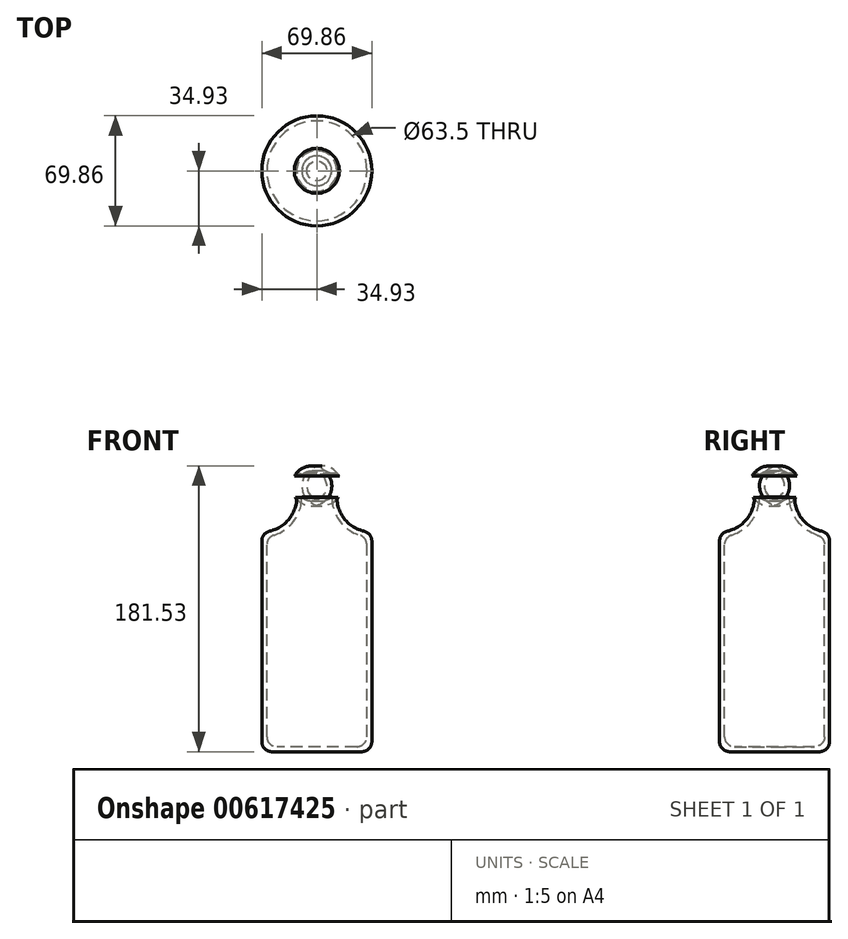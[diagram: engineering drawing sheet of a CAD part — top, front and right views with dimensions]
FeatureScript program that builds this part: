
annotation { "Feature Type Name" : "Feature", "Feature Type Description" : "" }
export const myFeature = defineFeature(function(context is Context, id is Id, definition is map)
    precondition{}
    {
        {
            var Q0;
            Q0=qCreatedBy(makeId("Front.planeOp"),FACE);
            var sketch = newSketch(context, id + "F0", { "sketchPlane" : qUnion([Q0])});
            skLineSegment(sketch, "E0", {"start": v(0, 0) * mm, "end": v(31.75, 0) * mm});
            skLineSegment(sketch, "E1", {"start": v(31.75, 0) * mm, "end": v(31.75, 133.35) * mm});
            skArc(sketch, "E2", {"start": v(9.52, 158.55) * mm, "mid": v(12.7, 165.65) * mm, "end": v(9.52, 172.75) * mm});
            skArc(sketch, "E3", {"start": v(9.52, 158.55) * mm, "mid": v(15.87, 141.75) * mm, "end": v(31.75, 133.35) * mm});
            skLineSegment(sketch, "E4", {"start": v(0, 176.65) * mm, "end": v(0, 0) * mm, "construction": true});
            skLineSegment(sketch, "E5.1", {"start": v(0, -3.18) * mm, "end": v(34.92, -3.18) * mm});
            skLineSegment(sketch, "E5.2", {"start": v(34.92, -3.17) * mm, "end": v(34.93, 136.33) * mm});
            skArc(sketch, "E5.3", {"start": v(12.74, 157.3) * mm, "mid": v(19.66, 142.4) * mm, "end": v(34.93, 136.33) * mm});
            skArc(sketch, "E5.4", {"start": v(12.74, 157.3) * mm, "mid": v(15.7, 167.73) * mm, "end": v(9.52, 176.65) * mm});
            skLineSegment(sketch, "E6", {"start": v(9.52, 172.75) * mm, "end": v(9.52, 176.65) * mm});
            skLineSegment(sketch, "E7", {"start": v(0, -3.18) * mm, "end": v(0, 0) * mm});
            skSolve(sketch);
        }
        {
            var Q0;
            Q0 = qSketchRegion(id + "F0", true);
            var Q1;
            Q1=sQuery(id+"F0.wireOp",EDGE,"E4");
            revolve(context, id + "F1", {"entities" : qUnion([Q0]), "axis" : qUnion([Q1]), "revolveType" : RevolveType.FULL});
        }
        {
            var Q0;
            Q0=makeQuery(id+"F1.opRevolve","SWEPT_EDGE",EDGE,{"disambiguationData":[OSD([sQuery(id+"F0.wireOp",EDGE,"E5.2"),sQuery(id+"F0.wireOp",EDGE,"E5.3")])]});
            fillet(context, id + "F2", {"entities" : qUnion([Q0]), "radius" : 6.35 * mm, "tangentPropagation" : true, "allowEdgeOverflow" : false});
        }
        {
            var Q0;
            Q0=makeQuery(id+"F1.opRevolve","SWEPT_EDGE",EDGE,{"disambiguationData":[OSD([sQuery(id+"F0.wireOp",EDGE,"E5.1"),sQuery(id+"F0.wireOp",EDGE,"E5.2")])]});
            fillet(context, id + "F3", {"entities" : qUnion([Q0]), "radius" : 6.35 * mm, "tangentPropagation" : true, "allowEdgeOverflow" : false});
        }
        {
            var Q0;
            Q0=makeQuery(id+"F1.opRevolve","SWEPT_EDGE",EDGE,{"disambiguationData":[OSD([sQuery(id+"F0.wireOp",EDGE,"E5.4"),sQuery(id+"F0.wireOp",EDGE,"E6")])]});
            fillet(context, id + "F4", {"entities" : qUnion([Q0]), "radius" : 3.17 * mm, "tangentPropagation" : true, "allowEdgeOverflow" : false});
        }
        {
            var Q0;
            Q0=makeQuery(id+"F1.opRevolve","SWEPT_EDGE",EDGE,{"disambiguationData":[OSD([sQuery(id+"F0.wireOp",EDGE,"E5.3"),sQuery(id+"F0.wireOp",EDGE,"E5.4")])]});
            fillet(context, id + "F5", {"entities" : qUnion([Q0]), "radius" : 3.17 * mm, "tangentPropagation" : true, "allowEdgeOverflow" : false});
        }
        {
            var Q0;
            Q0=makeQuery(id+"F1.opRevolve","SWEPT_EDGE",EDGE,{"disambiguationData":[OSD([sQuery(id+"F0.wireOp",EDGE,"E0"),sQuery(id+"F0.wireOp",EDGE,"E1")])]});
            fillet(context, id + "F6", {"entities" : qUnion([Q0]), "radius" : 6.35 * mm, "tangentPropagation" : true, "allowEdgeOverflow" : false});
        }
        {
            var Q0;
            Q0=makeQuery(id+"F1.opRevolve","SWEPT_EDGE",EDGE,{"disambiguationData":[OSD([sQuery(id+"F0.wireOp",EDGE,"E1"),sQuery(id+"F0.wireOp",EDGE,"E3")])]});
            fillet(context, id + "F7", {"entities" : qUnion([Q0]), "radius" : 6.35 * mm, "tangentPropagation" : true, "allowEdgeOverflow" : false});
        }
    });
